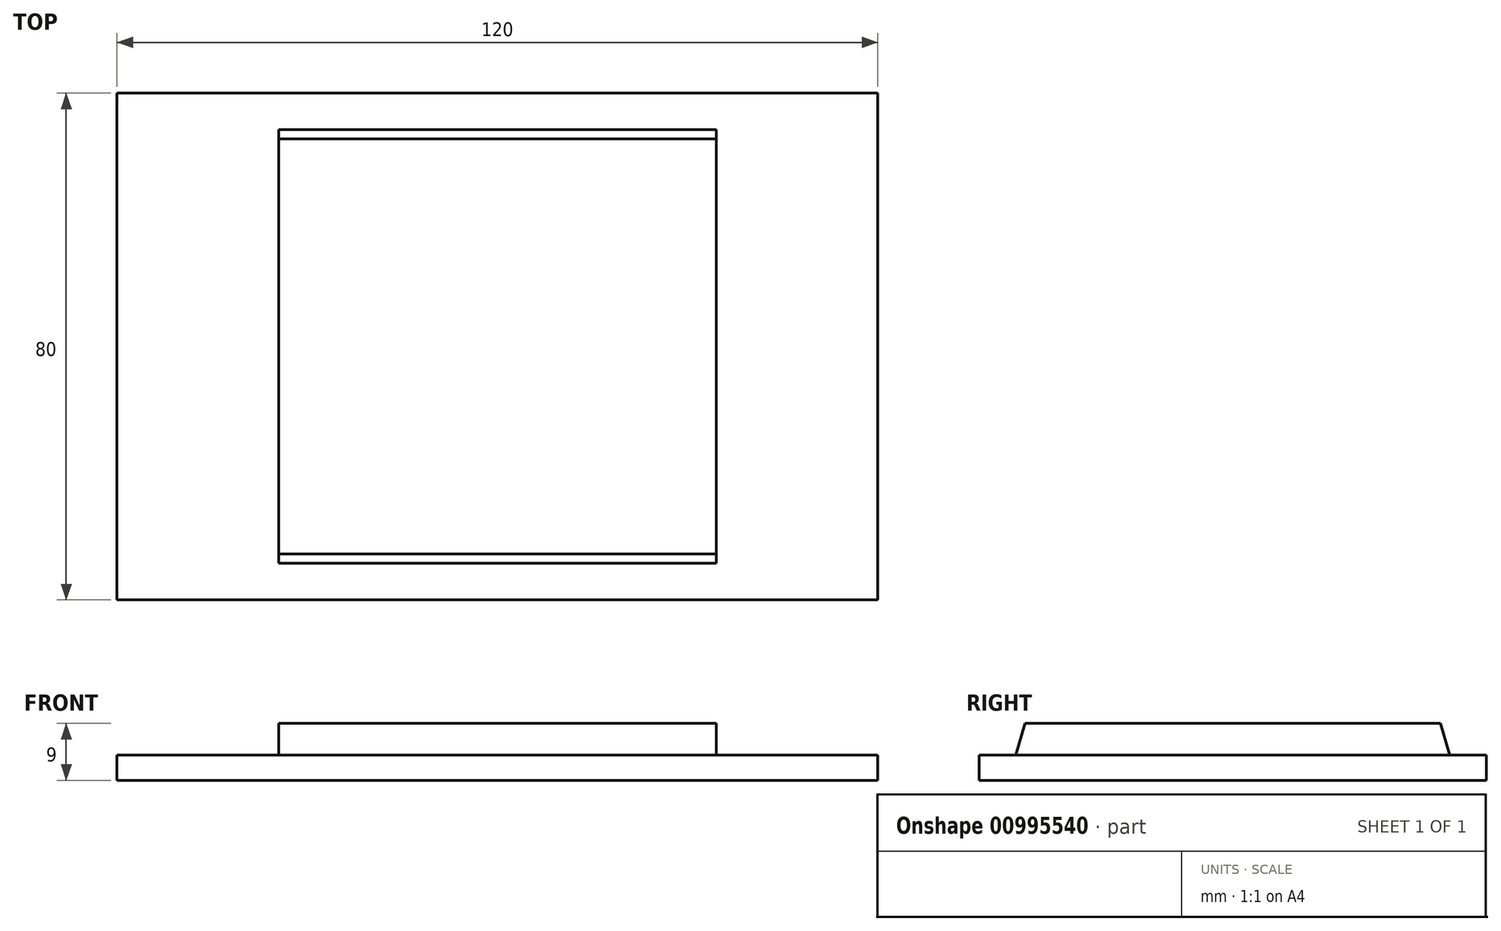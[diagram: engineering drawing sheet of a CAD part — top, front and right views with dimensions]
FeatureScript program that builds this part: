
annotation { "Feature Type Name" : "Feature", "Feature Type Description" : "" }
export const myFeature = defineFeature(function(context is Context, id is Id, definition is map)
    precondition{}
    {
        {
            var Q0;
            Q0=qCreatedBy(makeId("Top.planeOp"),FACE);
            var sketch = newSketch(context, id + "F0", { "sketchPlane" : qUnion([Q0])});
            skLineSegment(sketch, "E0.bottom", {"start": v(60, -40) * mm, "end": v(-60, -40) * mm});
            skLineSegment(sketch, "E0.top", {"start": v(60, 40) * mm, "end": v(-60, 40) * mm});
            skLineSegment(sketch, "E0.left", {"start": v(60, -40) * mm, "end": v(60, 40) * mm});
            skLineSegment(sketch, "E0.right", {"start": v(-60, -40) * mm, "end": v(-60, 40) * mm});
            skPoint(sketch, "E0.middle", {"position": v(0, 0) * mm});
            skSolve(sketch);
        }
        {
            var Q0;
            Q0=makeQuery(id+"F0.imprint","IMPRINT",FACE,{"disambiguationData":[TD([[makeQuery(id+"F0.imprint","IMPRINT",EDGE,{"derivedFrom":sQuery(id+"F0.wireOp",EDGE,"E0.bottom")}),-1.0]])]});
            extrude(context, id + "F1", {"entities" : qUnion([Q0]), "depth" : 4 * mm, "offsetDistance" : 25 * mm});
        }
        {
            var Q0;
            Q0=makeQuery(id+"F1.opExtrude","CAP_FACE",FACE,{"disambiguationData":[OSD([sQuery(id+"F0.wireOp",EDGE,"E0.bottom"),sQuery(id+"F0.wireOp",EDGE,"E0.top"),sQuery(id+"F0.wireOp",EDGE,"E0.left"),sQuery(id+"F0.wireOp",EDGE,"E0.right")])],"isStart":false});
            var sketch = newSketch(context, id + "F2", { "sketchPlane" : qUnion([Q0])});
            skLineSegment(sketch, "E1.bottom", {"start": v(34.5, 34.25) * mm, "end": v(-34.5, 34.25) * mm});
            skLineSegment(sketch, "E1.top", {"start": v(34.5, -34.25) * mm, "end": v(-34.5, -34.25) * mm});
            skLineSegment(sketch, "E1.left", {"start": v(34.5, 34.25) * mm, "end": v(34.5, -34.25) * mm});
            skLineSegment(sketch, "E1.right", {"start": v(-34.5, 34.25) * mm, "end": v(-34.5, -34.25) * mm});
            skPoint(sketch, "E1.middle", {"position": v(0, 0) * mm});
            skSolve(sketch);
        }
        {
            var Q0;
            Q0=makeQuery(id+"F2.imprint","IMPRINT",FACE,{"disambiguationData":[TD([[makeQuery(id+"F2.imprint","IMPRINT",EDGE,{"derivedFrom":sQuery(id+"F2.wireOp",EDGE,"E1.bottom")}),1.0]])]});
            extrude(context, id + "F3", {"entities" : qUnion([Q0]), "operationType" : NewBodyOperationType.ADD, "depth" : 5 * mm, "offsetDistance" : 25 * mm});
        }
        {
            var Q0;
            Q0=makeQuery(id+"F3.opExtrude","CAP_EDGE",EDGE,{"disambiguationData":[OSD([sQuery(id+"F2.wireOp",EDGE,"E1.bottom")])],"isStart":false});
            var Q1;
            Q1=makeQuery(id+"F3.opExtrude","CAP_EDGE",EDGE,{"disambiguationData":[OSD([sQuery(id+"F2.wireOp",EDGE,"E1.top")])],"isStart":false});
            chamfer(context, id + "F4", {"entities" : qUnion([Q0, Q1]), "chamferType" : ChamferType.TWO_OFFSETS, "width1" : 1.5 * mm, "oppositeDirection" : false, "width2" : 5 * mm, "tangentPropagation" : true});
        }
    });
